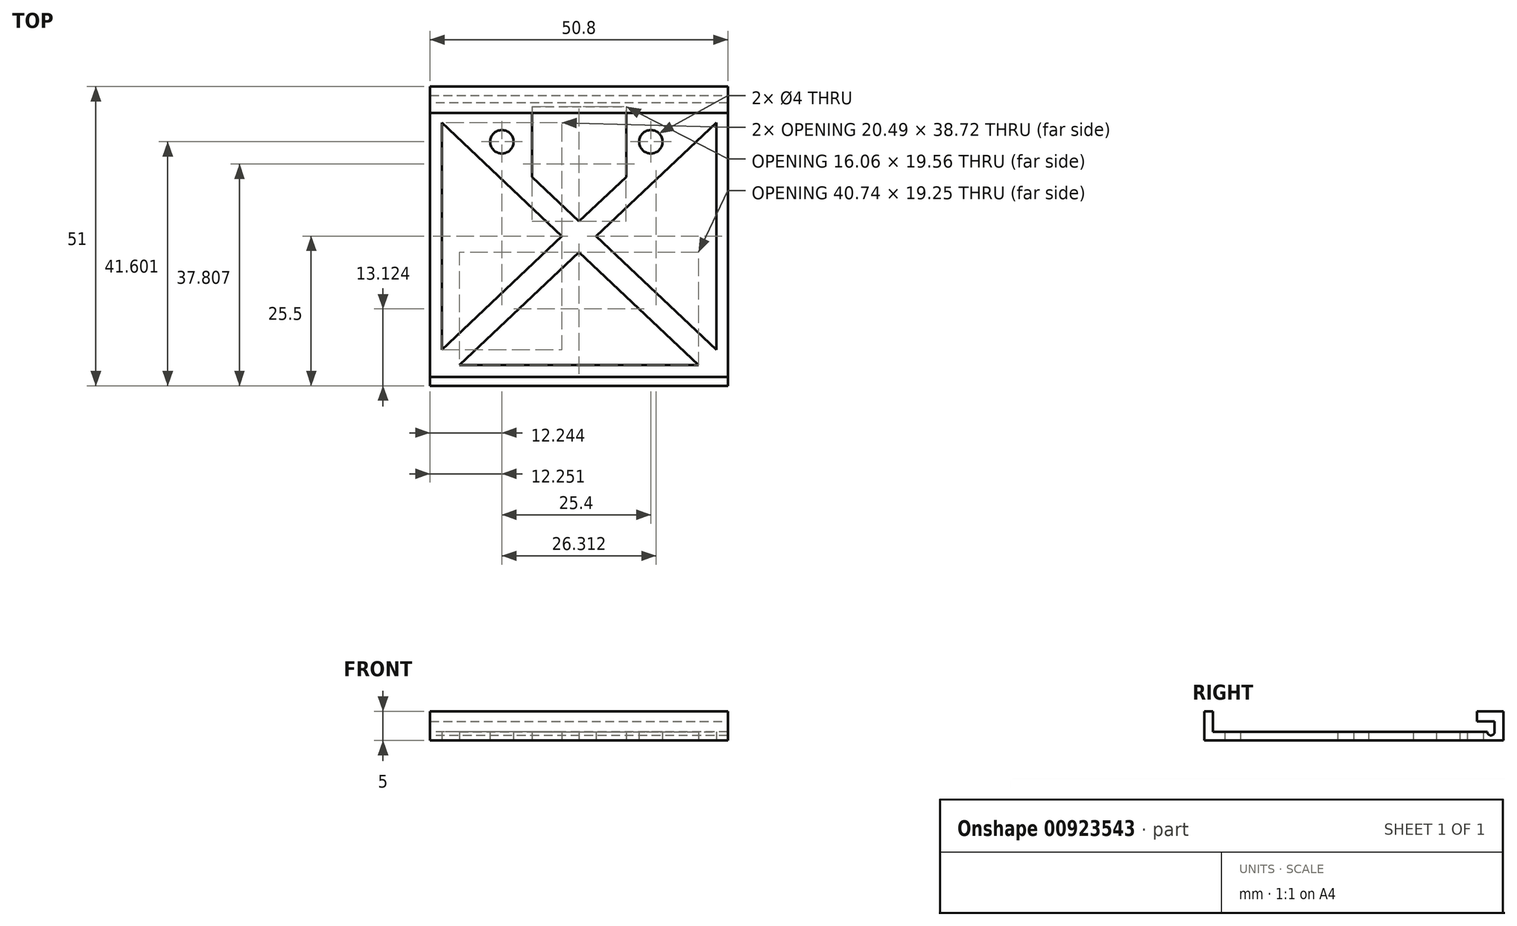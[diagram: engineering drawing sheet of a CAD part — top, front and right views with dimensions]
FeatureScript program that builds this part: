
annotation { "Feature Type Name" : "Feature", "Feature Type Description" : "" }
export const myFeature = defineFeature(function(context is Context, id is Id, definition is map)
    precondition{}
    {
        {
            var Q0;
            Q0=qCreatedBy(makeId("Top.planeOp"),FACE);
            var sketch = newSketch(context, id + "F0", { "sketchPlane" : qUnion([Q0])});
            skLineSegment(sketch, "E0.bottom", {"start": v(-25.4, 24) * mm, "end": v(25.4, 24) * mm});
            skLineSegment(sketch, "E0.top", {"start": v(-25.4, -24) * mm, "end": v(25.4, -24) * mm});
            skLineSegment(sketch, "E0.left", {"start": v(-25.4, 24) * mm, "end": v(-25.4, -24) * mm});
            skLineSegment(sketch, "E0.right", {"start": v(25.4, 24) * mm, "end": v(25.4, -24) * mm});
            skPoint(sketch, "E0.middle", {"position": v(0, 0) * mm});
            skLineSegment(sketch, "E1.bottom", {"start": v(-25.4, 25.5) * mm, "end": v(25.4, 25.5) * mm});
            skLineSegment(sketch, "E1.top", {"start": v(-25.4, -25.5) * mm, "end": v(25.4, -25.5) * mm});
            skLineSegment(sketch, "E1.left", {"start": v(-25.4, 25.5) * mm, "end": v(-25.4, -25.5) * mm});
            skLineSegment(sketch, "E1.right", {"start": v(25.4, 25.5) * mm, "end": v(25.4, -25.5) * mm});
            skCircle(sketch, "E2", {"center": v(-13.15, 16.1) * mm, "radius": 2 * mm});
            skCircle(sketch, "E3", {"center": v(12.25, 16.1) * mm, "radius": 2 * mm});
            skLineSegment(sketch, "E4", {"start": v(-25.4, -24) * mm, "end": v(0, 0) * mm});
            skLineSegment(sketch, "E5", {"start": v(0, 0) * mm, "end": v(25.4, -24) * mm});
            skLineSegment(sketch, "E6", {"start": v(0, 0) * mm, "end": v(-25.4, 24) * mm});
            skLineSegment(sketch, "E7", {"start": v(0, 0) * mm, "end": v(25.4, 24) * mm});
            skLineSegment(sketch, "E8.0", {"start": v(-2.91, 0) * mm, "end": v(-23.4, 19.36) * mm});
            skLineSegment(sketch, "E8.1", {"start": v(-23.4, -19.36) * mm, "end": v(-2.91, 0) * mm});
            skLineSegment(sketch, "E8.2", {"start": v(-23.4, 19.36) * mm, "end": v(-23.4, -19.36) * mm});
            skLineSegment(sketch, "E9.0", {"start": v(2.91, 0) * mm, "end": v(23.4, -19.36) * mm});
            skLineSegment(sketch, "E9.1", {"start": v(2.91, 0) * mm, "end": v(23.4, 19.36) * mm});
            skLineSegment(sketch, "E9.2", {"start": v(23.4, 19.36) * mm, "end": v(23.4, -19.36) * mm});
            skLineSegment(sketch, "E10.0", {"start": v(-20.37, -22) * mm, "end": v(0, -2.75) * mm});
            skLineSegment(sketch, "E10.1", {"start": v(-20.37, -22) * mm, "end": v(20.37, -22) * mm});
            skLineSegment(sketch, "E10.2", {"start": v(0, -2.75) * mm, "end": v(20.37, -22) * mm});
            skLineSegment(sketch, "E11.bottom", {"start": v(-8.03, 22.09) * mm, "end": v(8.03, 22.09) * mm});
            skLineSegment(sketch, "E11.left", {"start": v(-8.03, 22.09) * mm, "end": v(-8.03, 10.12) * mm});
            skLineSegment(sketch, "E11.right", {"start": v(8.03, 22.09) * mm, "end": v(8.03, 10.12) * mm});
            skPoint(sketch, "E11.middle", {"position": v(0, 16.1) * mm});
            skLineSegment(sketch, "E12", {"start": v(-8.03, 10.12) * mm, "end": v(0, 2.53) * mm});
            skLineSegment(sketch, "E13", {"start": v(0, 2.53) * mm, "end": v(8.03, 10.12) * mm});
            skSolve(sketch);
        }
        {
            var Q0;
            {var subQ1=sQuery(id+"F0.wireOp",EDGE,"E0.bottom");Q0=makeQuery(id+"F0.imprint","IMPRINT",FACE,{"disambiguationData":[TD([[makeQuery(id+"F0.imprint","IMPRINT",EDGE,{"derivedFrom":subQ1}),-1.0]])]});}
            var Q1;
            {var subQ2=sQuery(id+"F0.wireOp",EDGE,"E4");Q1=makeQuery(id+"F0.imprint","IMPRINT",FACE,{"disambiguationData":[TD([[makeQuery(id+"F0.imprint","IMPRINT",EDGE,{"derivedFrom":subQ2}),1.0]])]});}
            var Q2;
            Q2=makeQuery(id+"F0.imprint","IMPRINT",FACE,{"disambiguationData":[TD([[makeQuery(id+"F0.imprint","IMPRINT",EDGE,{"derivedFrom":sQuery(id+"F0.wireOp",EDGE,"E0.top")}),1.0]])]});
            var Q3;
            {var subQ2=sQuery(id+"F0.wireOp",EDGE,"E5");Q3=makeQuery(id+"F0.imprint","IMPRINT",FACE,{"disambiguationData":[TD([[makeQuery(id+"F0.imprint","IMPRINT",EDGE,{"derivedFrom":subQ2}),1.0]])]});}
            extrude(context, id + "F1", {"entities" : qUnion([Q0, Q1, Q2, Q3]), "depth" : 1.5 * mm, "offsetDistance" : 25 * mm});
        }
        {
            var Q0;
            {var subQ0=sQuery(id+"F0.wireOp",EDGE,"E0.top");Q0=makeQuery(id+"F0.imprint","IMPRINT",FACE,{"disambiguationData":[TD([[makeQuery(id+"F0.imprint","IMPRINT",EDGE,{"derivedFrom":subQ0}),-1.0]])]});}
            extrude(context, id + "F2", {"entities" : qUnion([Q0]), "operationType" : NewBodyOperationType.ADD, "depth" : 5 * mm, "offsetDistance" : 25 * mm});
        }
        {
            var Q0;
            {var subQ0=sQuery(id+"F0.wireOp",EDGE,"E0.bottom");Q0=makeQuery(id+"F0.imprint","IMPRINT",FACE,{"disambiguationData":[TD([[makeQuery(id+"F0.imprint","IMPRINT",EDGE,{"derivedFrom":subQ0}),1.0]])]});}
            extrude(context, id + "F3", {"entities" : qUnion([Q0]), "operationType" : NewBodyOperationType.ADD, "depth" : 5 * mm, "offsetDistance" : 25 * mm});
        }
        {
            var Q0;
            Q0=makeQuery(id+"F3.opExtrude","SWEPT_FACE",FACE,{"disambiguationData":[OSD([sQuery(id+"F0.wireOp",EDGE,"E0.bottom")])]});
            var sketch = newSketch(context, id + "F4", { "sketchPlane" : qUnion([Q0])});
            skLineSegment(sketch, "E14", {"start": v(-25.4, 3.25) * mm, "end": v(25.4, 3.25) * mm});
            skSolve(sketch);
        }
        {
            var Q0;
            Q0 = qSketchRegion(id + "F4", true);
            var Q1;
            {var subQ0=sQuery(id+"F4.wireOp",EDGE,"E14");Q1=makeQuery(id+"F4.imprint","IMPRINT",FACE,{"disambiguationData":[TD([[makeQuery(id+"F4.imprint","IMPRINT",EDGE,{"derivedFrom":subQ0}),1.0]])]});}
            extrude(context, id + "F5", {"entities" : qUnion([Q0, Q1]), "operationType" : NewBodyOperationType.ADD, "depth" : 3 * mm, "offsetDistance" : 25 * mm});
        }
        {
            var Q0;
            {var subQ0=sQuery(id+"F0.wireOp",EDGE,"E1.left");Q0=makeQuery(id+"F5.boolean.opBoolean","MERGE",FACE,{"derivedFrom":[makeQuery(id+"F3.boolean.opBoolean","MERGE",FACE,{"derivedFrom":[makeQuery(id+"F2.boolean.opBoolean","MERGE",FACE,{"derivedFrom":[makeQuery(id+"F1.opExtrude","SWEPT_FACE",FACE,{"disambiguationData":[OSD([subQ0])]}),makeQuery(id+"F2.opExtrude","SWEPT_FACE",FACE,{"disambiguationData":[OSD([subQ0])]})]}),makeQuery(id+"F3.opExtrude","SWEPT_FACE",FACE,{"disambiguationData":[OSD([subQ0])]})]}),makeQuery(id+"F5.opExtrude","SWEPT_FACE",FACE,{"disambiguationData":[OSD([sQuery(id+"F0.wireOp",EDGE,"E0.bottom"),subQ0])]})]});}
            var sketch = newSketch(context, id + "F6", { "sketchPlane" : qUnion([Q0])});
            skCircle(sketch, "E15", {"center": v(-23.37, 1.5) * mm, "radius": 0.62 * mm});
            skSolve(sketch);
        }
        {
            var Q0;
            {var subQ0=sQuery(id+"F6.wireOp",EDGE,"E15");var subQ1=sQuery(id+"F0.wireOp",EDGE,"E1.left");var subQ2=makeQuery(id+"F1.opExtrude","CAP_EDGE",EDGE,{"disambiguationData":[OSD([subQ1])],"isStart":false});var subQ4=makeQuery(id+"F6.imprint","INTERSECT",VERTEX,{"derivedFrom":[subQ2,subQ0]});Q0=makeQuery(id+"F6.imprint","IMPRINT",FACE,{"disambiguationData":[TD([[makeQuery(id+"F6.imprint","IMPRINT",EDGE,{"disambiguationData":[TD([[subQ4,1.0]])],"derivedFrom":subQ0}),1.0]])]});}
            extrude(context, id + "F7", {"entities" : qUnion([Q0]), "operationType" : NewBodyOperationType.REMOVE, "endBound" : BoundingType.THROUGH_ALL, "oppositeDirection" : true, "depth" : 25 * mm, "offsetDistance" : 25 * mm});
        }
    });
